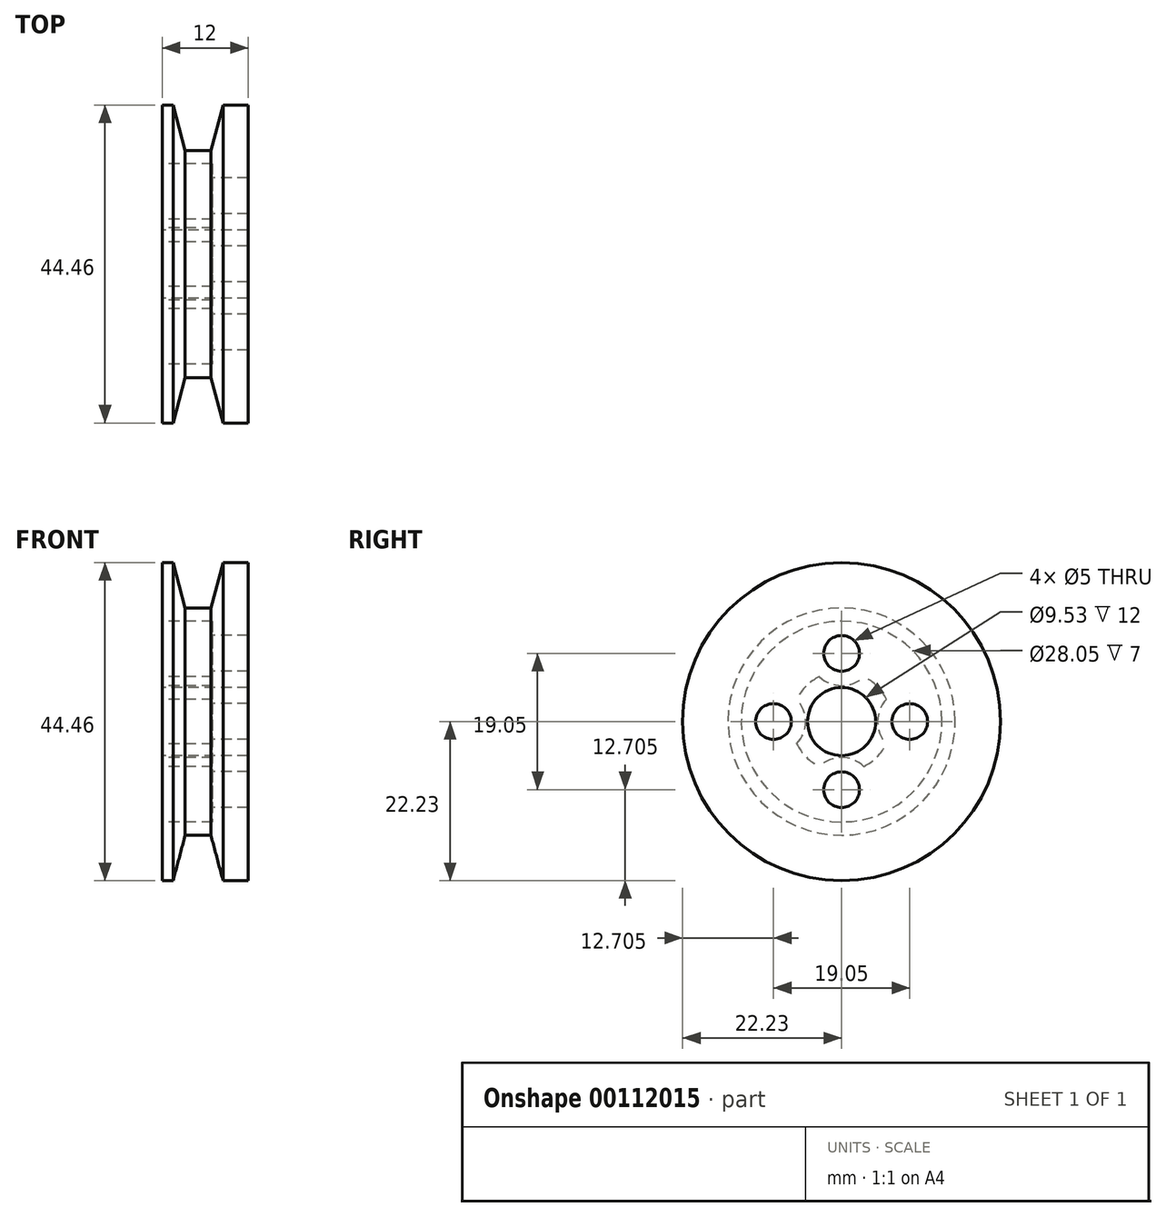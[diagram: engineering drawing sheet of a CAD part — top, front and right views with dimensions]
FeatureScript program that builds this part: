
annotation { "Feature Type Name" : "Feature", "Feature Type Description" : "" }
export const myFeature = defineFeature(function(context is Context, id is Id, definition is map)
    precondition{}
    {
        {
            var Q0;
            Q0=qCreatedBy(makeId("Front.planeOp"),FACE);
            var sketch = newSketch(context, id + "F0", { "sketchPlane" : qUnion([Q0])});
            skLineSegment(sketch, "E0", {"start": v(0, 0) * mm, "end": v(0, 22.23) * mm});
            skLineSegment(sketch, "E1", {"start": v(0, 22.23) * mm, "end": v(1.5, 22.23) * mm});
            skLineSegment(sketch, "E2", {"start": v(1.5, 22.23) * mm, "end": v(3.2, 15.88) * mm});
            skLineSegment(sketch, "E3", {"start": v(3.2, 15.88) * mm, "end": v(6.8, 15.88) * mm});
            skLineSegment(sketch, "E4", {"start": v(6.8, 15.88) * mm, "end": v(8.5, 22.23) * mm});
            skLineSegment(sketch, "E5", {"start": v(8.5, 22.23) * mm, "end": v(10, 22.23) * mm});
            skLineSegment(sketch, "E6", {"start": v(10, 22.23) * mm, "end": v(10, 0) * mm});
            skLineSegment(sketch, "E7", {"start": v(10, 0) * mm, "end": v(0, 0) * mm});
            skLineSegment(sketch, "E8", {"start": v(1.83, 21.04) * mm, "end": v(8.18, 21.04) * mm, "construction": true});
            skLineSegment(sketch, "E9", {"start": v(2.91, 16.98) * mm, "end": v(7.09, 16.98) * mm, "construction": true});
            skPoint(sketch, "E10", {"position": v(5, 15.88) * mm});
            skSolve(sketch);
        }
        {
            var Q0;
            Q0 = qSketchRegion(id + "F0", true);
            var Q1;
            Q1=sQuery(id+"F0.wireOp",EDGE,"E7");
            revolve(context, id + "F1", {"entities" : qUnion([Q0]), "axis" : qUnion([Q1]), "revolveType" : RevolveType.FULL});
        }
        {
            var Q0;
            Q0=makeQuery(id+"F1.opRevolve","SWEPT_FACE",FACE,{"disambiguationData":[OSD([sQuery(id+"F0.wireOp",EDGE,"E0")])]});
            var sketch = newSketch(context, id + "F2", { "sketchPlane" : qUnion([Q0])});
            skCircle(sketch, "E11", {"center": v(0, 0) * mm, "radius": 9.53 * mm, "construction": true});
            skCircle(sketch, "E12", {"center": v(0, 9.53) * mm, "radius": 2.5 * mm});
            skCircle(sketch, "E13", {"center": v(9.53, 0) * mm, "radius": 2.5 * mm});
            skCircle(sketch, "E14", {"center": v(0, -9.53) * mm, "radius": 2.5 * mm});
            skCircle(sketch, "E15", {"center": v(-9.53, 0) * mm, "radius": 2.5 * mm});
            skCircle(sketch, "E16", {"center": v(0, 0) * mm, "radius": 4.76 * mm});
            skSolve(sketch);
        }
        {
            var Q0;
            Q0 = qSketchRegion(id + "F2", true);
            extrude(context, id + "F3", {"entities" : qUnion([Q0]), "operationType" : NewBodyOperationType.REMOVE, "endBound" : BoundingType.THROUGH_ALL, "oppositeDirection" : true, "depth" : 25 * mm});
        }
        {
            var Q0;
            Q0=makeQuery(id+"F1.opRevolve","SWEPT_FACE",FACE,{"disambiguationData":[OSD([sQuery(id+"F0.wireOp",EDGE,"E0")])]});
            var sketch = newSketch(context, id + "F4", { "sketchPlane" : qUnion([Q0])});
            skPoint(sketch, "E17", {"position": v(0, 9.53) * mm});
            skPoint(sketch, "E18", {"position": v(9.53, 0) * mm});
            skPoint(sketch, "E19", {"position": v(-9.53, 0) * mm});
            skPoint(sketch, "E20", {"position": v(0, -9.53) * mm});
            skSolve(sketch);
        }
        {
            var Q0;
            Q0=sQuery(id+"F4.wireOp",VERTEX,"E17");
            var Q1;
            Q1=sQuery(id+"F4.wireOp",VERTEX,"E19");
            var Q2;
            Q2=sQuery(id+"F4.wireOp",VERTEX,"E20");
            var Q3;
            Q3=sQuery(id+"F4.wireOp",VERTEX,"E18");
            var Q4;
            Q4=makeQuery(id+"F1.opRevolve","SWEPT_BODY",BODY,{"disambiguationData":[OSD([sQuery(id+"F0.wireOp",EDGE,"E0"),sQuery(id+"F0.wireOp",EDGE,"E1"),sQuery(id+"F0.wireOp",EDGE,"E2"),sQuery(id+"F0.wireOp",EDGE,"E3"),sQuery(id+"F0.wireOp",EDGE,"E4"),sQuery(id+"F0.wireOp",EDGE,"E5"),sQuery(id+"F0.wireOp",EDGE,"E6"),sQuery(id+"F0.wireOp",EDGE,"E7")])]});
            hole(context, id + "F5", {"style" : HoleStyle.C_BORE, "endStyle" : HoleEndStyle.THROUGH, "holeDiameter" : 5 * mm, "cBoreDiameter" : 9 * mm, "cBoreDepth" : 7 * mm, "locations" : qUnion([Q0, Q1, Q2, Q3]), "scope" : qUnion([Q4]), "isTappedThrough" : true});
        }
        {
            var Q0;
            Q0=makeQuery(id+"F1.opRevolve","SWEPT_FACE",FACE,{"disambiguationData":[OSD([sQuery(id+"F0.wireOp",EDGE,"E0")])]});
            var sketch = newSketch(context, id + "F6", { "sketchPlane" : qUnion([Q0])});
            skCircle(sketch, "E21", {"center": v(0, 0) * mm, "radius": 7 * mm});
            skCircle(sketch, "E22", {"center": v(0, 0) * mm, "radius": 14.02 * mm});
            skSolve(sketch);
        }
        {
            var Q0;
            Q0 = qSketchRegion(id + "F6", true);
            extrude(context, id + "F7", {"entities" : qUnion([Q0]), "operationType" : NewBodyOperationType.REMOVE, "oppositeDirection" : true, "depth" : 7 * mm});
        }
        {
            var Q0;
            Q0=makeQuery(id+"F1.opRevolve","SWEPT_FACE",FACE,{"disambiguationData":[OSD([sQuery(id+"F0.wireOp",EDGE,"E6")])]});
            extrude(context, id + "F8", {"entities" : qUnion([Q0]), "operationType" : NewBodyOperationType.ADD, "depth" : 2 * mm});
        }
    });
